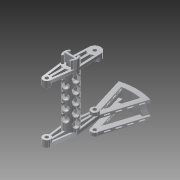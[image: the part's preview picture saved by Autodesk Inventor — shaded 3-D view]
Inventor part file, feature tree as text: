
AUTODESK INVENTOR PART (.ipt)
format: ipt  version: 2014 (Build 180170000, 170)  size: 1,212,416 bytes
history: native  units: mm
features: extrude x13, sketch x8, fillet x3, plane x1, chamfer x1, mirror x1, pattern_linear x1
ambient origin geometry x8: Origin, YZ Plane, XZ Plane, XY Plane, X Axis, Y Axis, Z Axis, Center Point
bodies: Solid1 (feature_tree)
feature tree (28):
  sketch  "Sketch1"  dims[d2=4.0mm d3=6.35mm]
  extrude  "Extrusion1"  Depth=6.35mm
  extrude  "Extrusion2"  Depth=13.0mm
  extrude  "Extrusion3"  Depth=4.0mm
  plane  "Work Plane1"
  extrude  "Extrusion4"  Depth=2.0mm
  extrude  "Extrusion5"  Depth=2.0mm
  extrude  "Extrusion6"  Depth=45.0mm
  extrude  "Extrusion7"  Depth=4.0mm
  extrude  "Extrusion8"  Depth=2.0mm
  extrude  "Extrusion9"  Depth=2.0mm
  extrude  "Extrusion10"  Depth=10.0mm
  fillet  "Fillet1"  Radius=6.0mm
  fillet  "Fillet2"  Radius=12.0mm
  extrude  "Extrusion11"  TaperAngle=0.0deg  [1 undecoded]
  fillet  "Fillet3"  Radius=108.0mm
  extrude  "Extrusion12"  Depth=10.0mm
  chamfer  "Chamfer1"  Distance=5.0mm
  sketch  "Sketch7"  dims[d14=6.5mm d15=45.0mm]
  sketch  "Sketch8"  dims[d16=6.35mm d17=4.0mm]
  extrude  "Extrusion13"  Depth=10.0mm
  mirror  "Mirror1"
  pattern_linear  "Rectangular Pattern2"  Spacing1=5.0mm  [1 undecoded]
  sketch  "Sketch3"  dims[d5=13.0mm d7=4.0mm]
  sketch  "Sketch4"  dims[d8=4.0mm d9=4.0mm]
  sketch  "Sketch5"  dims[d10=4.0mm d11=2.0mm]
  sketch  "Sketch6"  dims[d12=2.0mm d13=4.0mm]
  sketch  "Sketch9"  dims[d18=4.0mm d19=2.0mm d20=2.0mm d21=45.0mm d22=6.0mm d23=0.0mm d24=12.0mm d25=0.0mm d27=0.0mm d28=108.0mm d31=10.0mm d34=5.0mm d35=5.0mm d36=5.0mm d37=5.0mm d38=10.0mm d39=45.0deg d40=4.0mm d41=4.0mm d42=4.0mm d43=2.0mm d44=4.0mm d45=6.0mm d46=0.0mm d47=12.0mm d48=0.0mm d49=10.0mm d50=10.0mm d51=30.0mm d52=30.0mm d53=10.0mm d54=62.0mm d55=6.0mm d56=0.0mm d57=27.0mm d58=0.0mm d59=21.0mm d60=0.0mm d62=6.0mm d63=0.0mm d64=14.0mm d65=30.0mm d66=0.0mm d70=14.0mm d71=14.0mm d72=14.0mm d73=14.0mm d74=4.333333mm d75=4.333333mm d76=4.333333mm d77=4.333333mm d78=4.333333mm d79=4.333333mm d80=13.0mm d81=13.0mm d82=13.0mm d83=13.0mm d84=13.0mm d85=13.0mm d86=14.0mm d87=4.333333mm d88=14.0mm d89=14.0mm d90=14.0mm d91=4.333333mm d92=4.333333mm d93=26.5mm d94=26.5mm d95=30.0mm d96=0.0mm d97=1.0mm d98=1.0mm d99=4.0mm d100=2.0mm d101=2.0mm d102=45.0deg d103=45.0deg d104=15.0mm d105=0.0mm d106=1.0mm d107=32.0mm d108=26.0mm d109=7.5mm d110=8.774964mm d111=8.774964mm d112=4.0mm d113=10.0mm d114=0.0mm d115=90.0mm d116=6.0mm d117=2.0mm d118=45.0deg d119=150.0mm d120=2.0mm d121=12.763383mm d122=12.763383mm d123=7.433393mm d124=7.433393mm d125=7.433393mm d126=10.0mm d127=10.0mm d128=10.0mm d129=10.0mm d130=7.433393mm d131=7.433393mm d132=2.0mm d133=2.0mm d134=10.0mm d135=0.0mm d136=20.0mm d138=27.0mm]
note: 2 required parameter values undecoded (feature->parameter linkage not recoverable at this tier; creation-order binding heuristic only, values carry confidence <= 0.55)
